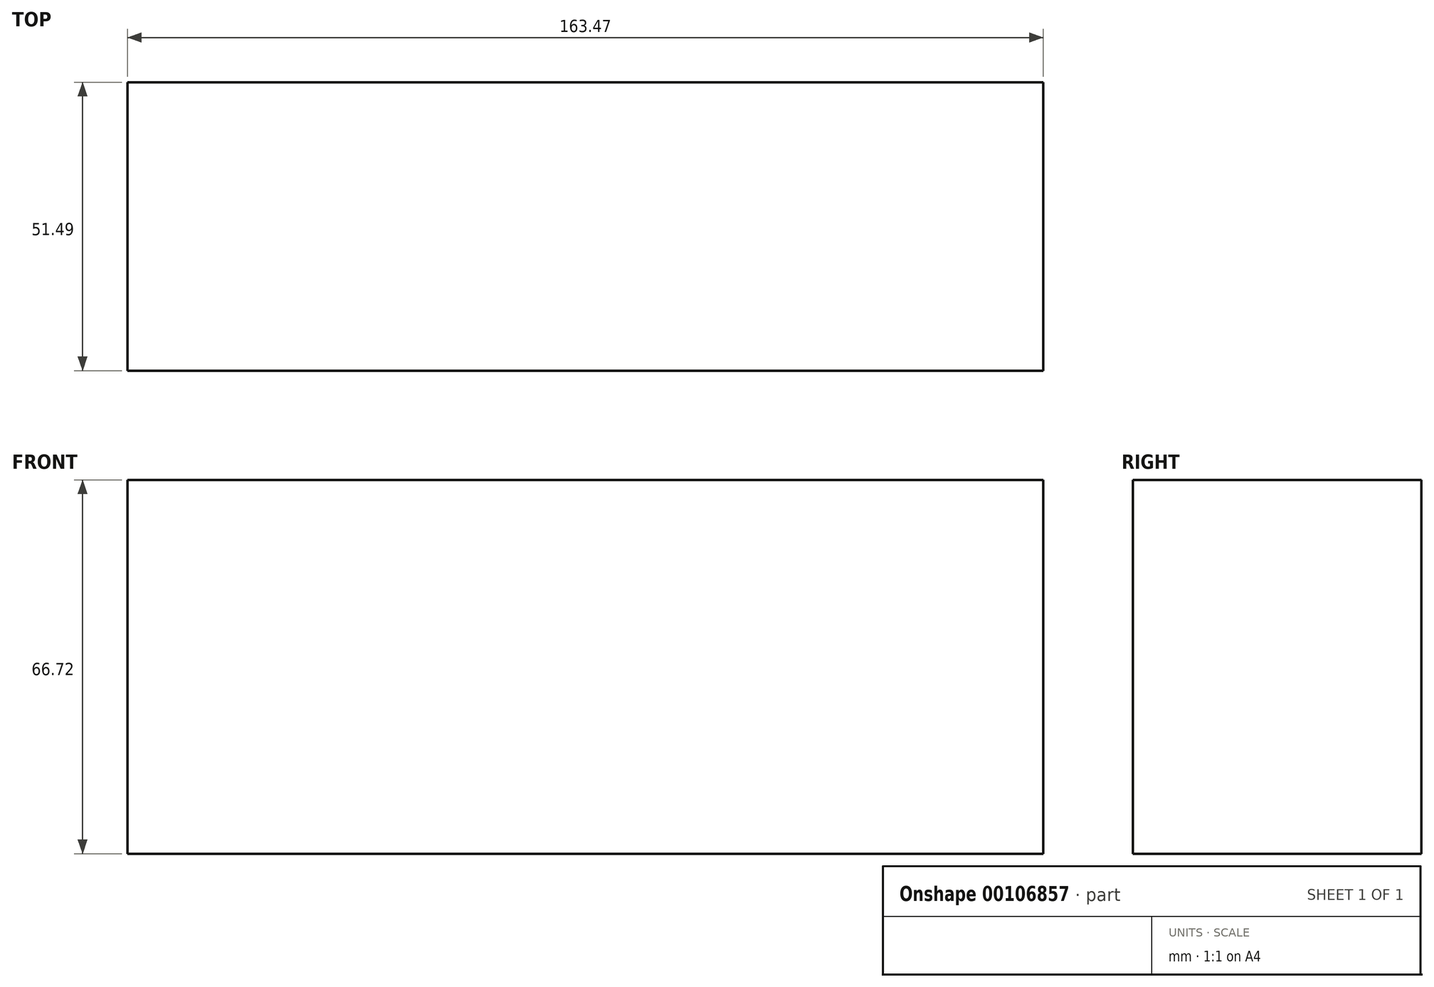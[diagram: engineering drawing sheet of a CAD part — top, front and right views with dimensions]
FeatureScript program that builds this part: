
annotation { "Feature Type Name" : "Feature", "Feature Type Description" : "" }
export const myFeature = defineFeature(function(context is Context, id is Id, definition is map)
    precondition{}
    {
        {
            var Q0;
            Q0=qCreatedBy(makeId("Top.planeOp"),FACE);
            var sketch = newSketch(context, id + "F0", { "sketchPlane" : qUnion([Q0])});
            skLineSegment(sketch, "E0.bottom", {"start": v(-130.22, -74.19) * mm, "end": v(-293.69, -74.19) * mm});
            skLineSegment(sketch, "E0.top", {"start": v(-130.22, -22.7) * mm, "end": v(-293.69, -22.7) * mm});
            skLineSegment(sketch, "E0.left", {"start": v(-130.22, -74.19) * mm, "end": v(-130.22, -22.7) * mm});
            skLineSegment(sketch, "E0.right", {"start": v(-293.69, -74.19) * mm, "end": v(-293.69, -22.7) * mm});
            skSolve(sketch);
        }
        {
            var Q0;
            Q0=makeQuery(id+"F0.imprint","IMPRINT",FACE,{"disambiguationData":[TD([[makeQuery(id+"F0.imprint","IMPRINT",EDGE,{"derivedFrom":sQuery(id+"F0.wireOp",EDGE,"E0.bottom")}),-1.0]])]});
            extrude(context, id + "F1", {"entities" : qUnion([Q0]), "depth" : 66.72 * mm});
        }
    });
